# Revit family: Daloc S30 Pardörr
name_source: partatom
category: Doors
revit_build: Autodesk Revit LT 2017 (Build: 20160225_1515(x64)
units: mm (PartAtom-declared; Revit-internal decimal feet)

## family parameters
Always vertical = Yes
Cut with Voids When Loaded = No
Host = Wall
OmniClass Number = 23.30.10.00
OmniClass Title = Doors
Room Calculation Point = No
Shared = No

## types (4) — shared parameters
Frame Projection Ext. = 25 mm  [stored 0.082021 ft]
Frame Projection Int. = 25 mm  [stored 0.082021 ft]
Frame Width = 75 mm  [stored 0.246063 ft]
Function = Interior
Wall Closure = By host

## per-type parameters (varying)
| type | Height | Modulbredd | Modulhöjd | Width |
| Pardörr 15x21 | 2100 mm | 15 | 21 | 1500 mm |
| Pardörr 18x21 | 2100 mm | 18 | 21 | 1800 mm |
| Pardörr 18x24 | 2400 mm | 18 | 24 | 1800 mm |
| Pardörr 21x24 | 2400 mm | 21 | 24 | 2100 mm |

note: [stored X ft] marks values corroborated as IEEE doubles in the binary element streams (Revit-internal decimal feet)

## geometry (parser evidence)
native form markers: Sweep x12
no freeform markers — native parametric forms only
